# Revit family: 201_RATT-_
name_source: partatom
category: Air Terminals
units: mm (PartAtom-declared; Revit-internal decimal feet)

## family parameters
Always vertical = Yes
Cut with Voids When Loaded = No
Part Type = Normal
Room Calculation Point = Yes
Round Connector Dimension = Use Diameter
Shared = No
Work Plane-Based = No

## types (5) — shared parameters
CAT0 = Yes
CAT1 = Yes
CAT2 = No
CL_Location_5000 = 5000 mm
Description = Square air diffuser with balancing plenum box
H1 = 70 mm  [stored 0.229659 ft]
H2 = 2 mm  [stored 0.00656168 ft]
L_ARR = 400 mm
Manufacturer = Climecon
QmdConnectorList = 201;D
URL = www.climecon.fi
W_ARR = 400 mm
XRefLineVPlnId = 7453
YRefLineVPlnId = 7456
magiPartTypeId = 201
magiProductFamilyId = RATT-*
zero-valued in all types: CLBTZ, H_ARR, MC_Default_elevation

## per-type parameters (varying)
| type | A | A1 | A2 | B1 | C | CLD | D | H3 | H4 | H5 | L1 | L2 | L3 | S1 | S1__ve | S2 | S2_End__ve | S2__ve |
| RATT-100 | 450 mm | 225 mm  [stored 0.738189 ft] | 225 mm  [stored 0.738189 ft] | 135 mm  [stored 0.442913 ft] | 110 mm  [stored 0.360892 ft] | 160 mm  [stored 0.524934 ft] | 100 mm | 136 mm  [stored 0.446194 ft] | 138 mm  [stored 0.452756 ft] | 70 mm  [stored 0.229659 ft] | 340 mm | 105 mm  [stored 0.344488 ft] | 335 mm | 15 mm  [stored 0.0492126 ft] | -15 mm | 29 mm | -44 mm | -29 mm |
| RATT-250 | 595 mm | 298 mm | 298 mm | 275 mm | 230 mm  [stored 0.754593 ft] | 400 mm | 250 mm | 286 mm | 288 mm | 145 mm  [stored 0.475722 ft] | 550 mm | 225 mm  [stored 0.738189 ft] | 545 mm | 22 mm | -22 mm  [stored -0.0721785 ft] | 43 mm | -65 mm | -43 mm |
| RATT-200 | 595 mm | 298 mm | 298 mm | 225 mm  [stored 0.738189 ft] | 187 mm  [stored 0.613517 ft] | 315 mm | 200 mm | 236 mm  [stored 0.774278 ft] | 238 mm  [stored 0.78084 ft] | 120 mm  [stored 0.393701 ft] | 443 mm | 182 mm  [stored 0.597113 ft] | 438 mm | 22 mm | -22 mm  [stored -0.0721785 ft] | 43 mm | -65 mm | -43 mm |
| RATT-160 | 595 mm | 298 mm | 298 mm | 200 mm  [stored 0.656168 ft] | 155 mm  [stored 0.50853 ft] | 250 mm  [stored 0.82021 ft] | 160 mm | 196 mm  [stored 0.643045 ft] | 198 mm  [stored 0.649606 ft] | 100 mm  [stored 0.328084 ft] | 395 mm | 150 mm  [stored 0.492126 ft] | 390 mm | 22 mm | -22 mm  [stored -0.0721785 ft] | 43 mm | -65 mm | -43 mm |
| RATT-125 | 450 mm | 225 mm  [stored 0.738189 ft] | 225 mm  [stored 0.738189 ft] | 170 mm  [stored 0.557743 ft] | 130 mm  [stored 0.426509 ft] | 200 mm  [stored 0.656168 ft] | 125 mm | 161 mm  [stored 0.528215 ft] | 163 mm  [stored 0.534777 ft] | 83 mm | 360 mm | 125 mm  [stored 0.410105 ft] | 355 mm | 15 mm  [stored 0.0492126 ft] | -15 mm | 29 mm | -44 mm | -29 mm |

note: column(s) folded — value = type name in every type: magiProductCode, magiProductId

note: [stored X ft] marks values corroborated as IEEE doubles in the binary element streams (Revit-internal decimal feet)

## geometry (parser evidence)
native form markers: Sweep x1
no freeform markers — native parametric forms only
